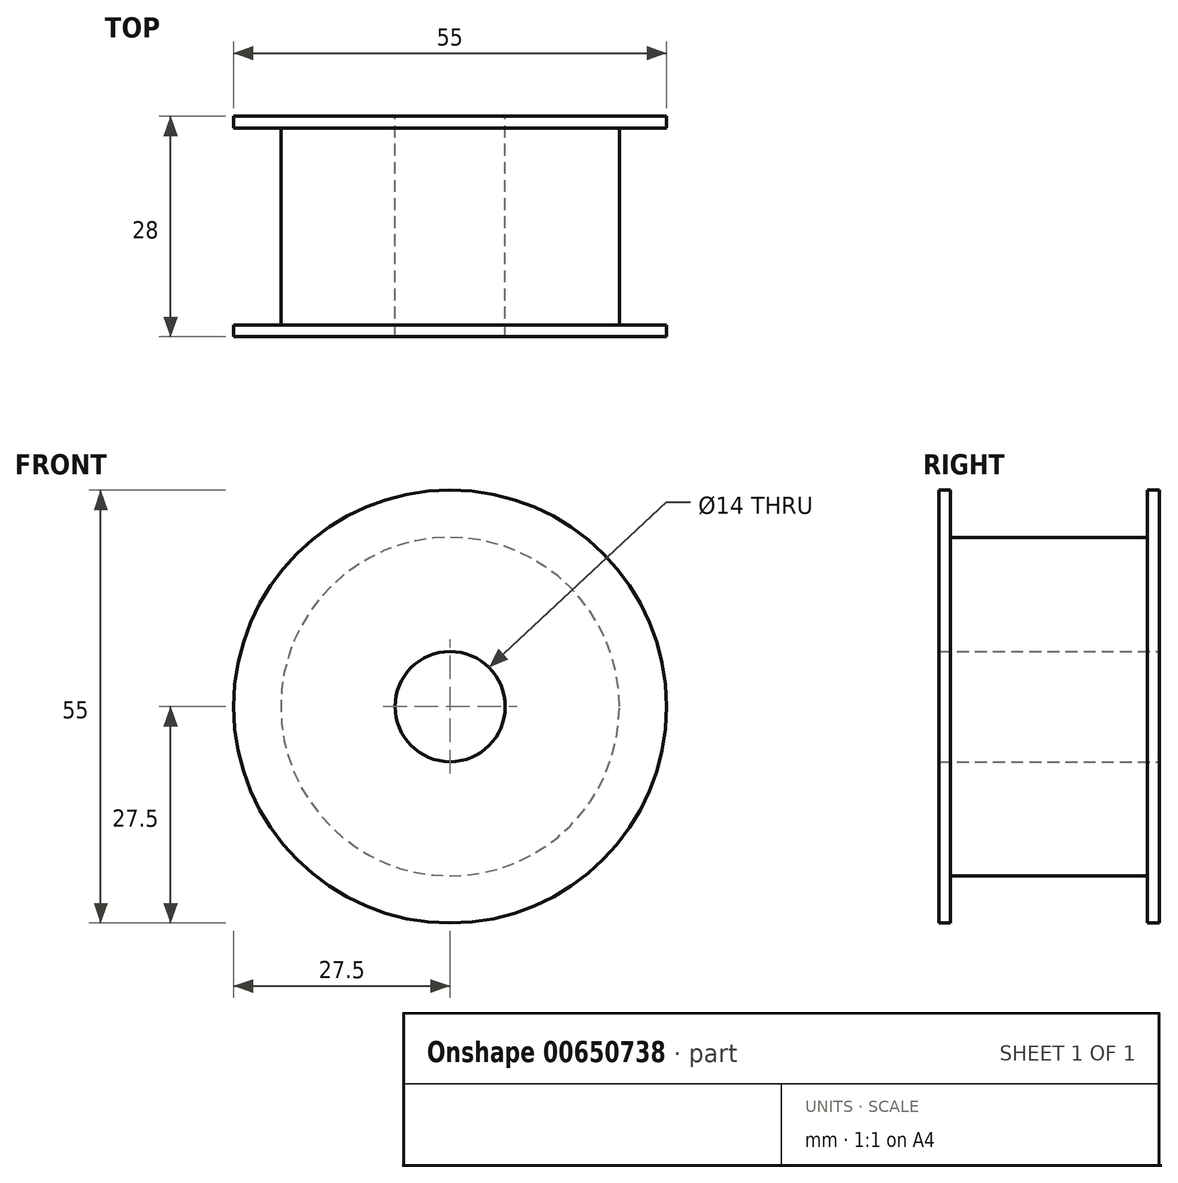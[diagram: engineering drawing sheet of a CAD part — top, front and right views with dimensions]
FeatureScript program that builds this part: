
annotation { "Feature Type Name" : "Feature", "Feature Type Description" : "" }
export const myFeature = defineFeature(function(context is Context, id is Id, definition is map)
    precondition{}
    {
        {
            var Q0;
            Q0=qCreatedBy(makeId("Front.planeOp"),FACE);
            var sketch = newSketch(context, id + "F0", { "sketchPlane" : qUnion([Q0])});
            skCircle(sketch, "E0", {"center": v(0, 0) * mm, "radius": 27.5 * mm});
            skSolve(sketch);
        }
        {
            var Q0;
            Q0 = qSketchRegion(id + "F0", true);
            extrude(context, id + "F1", {"entities" : qUnion([Q0]), "depth" : 28 * mm, "offsetDistance" : 25 * mm});
        }
        {
            var Q0;
            Q0=qCreatedBy(makeId("Right.planeOp"),FACE);
            var sketch = newSketch(context, id + "F2", { "sketchPlane" : qUnion([Q0])});
            skLineSegment(sketch, "E1.0", {"start": v(-28, -27.5) * mm, "end": v(-28, 27.5) * mm});
            skLineSegment(sketch, "E1.1", {"start": v(0, -27.5) * mm, "end": v(0, 27.5) * mm});
            skLineSegment(sketch, "E2", {"start": v(0, 0) * mm, "end": v(-28, 0) * mm, "construction": true});
            skLineSegment(sketch, "E3.bottom", {"start": v(-26.5, 27.5) * mm, "end": v(-1.5, 27.5) * mm});
            skLineSegment(sketch, "E3.top", {"start": v(-26.5, 21.5) * mm, "end": v(-1.5, 21.5) * mm});
            skLineSegment(sketch, "E3.left", {"start": v(-26.5, 27.5) * mm, "end": v(-26.5, 21.5) * mm});
            skLineSegment(sketch, "E3.right", {"start": v(-1.5, 27.5) * mm, "end": v(-1.5, 21.5) * mm});
            skPoint(sketch, "E4", {"position": v(-14, 21.5) * mm});
            skPoint(sketch, "E5", {"position": v(-14, 0) * mm});
            skSolve(sketch);
        }
        {
            var Q0;
            Q0 = qSketchRegion(id + "F2", true);
            var Q1;
            Q1=makeQuery(id+"F1.opExtrude","SWEPT_FACE",FACE,{"disambiguationData":[OSD([sQuery(id+"F0.wireOp",EDGE,"E0")])]});
            revolve(context, id + "F3", {"operationType" : NewBodyOperationType.REMOVE, "entities" : qUnion([Q0]), "axis" : qUnion([Q1]), "revolveType" : RevolveType.FULL, "oppositeDirection" : true});
        }
        {
            var Q0;
            Q0=qCreatedBy(makeId("Front.planeOp"),FACE);
            var sketch = newSketch(context, id + "F4", { "sketchPlane" : qUnion([Q0])});
            skCircle(sketch, "E6", {"center": v(0, 0) * mm, "radius": 7 * mm});
            skSolve(sketch);
        }
        {
            var Q0;
            Q0 = qSketchRegion(id + "F4", true);
            extrude(context, id + "F5", {"entities" : qUnion([Q0]), "operationType" : NewBodyOperationType.REMOVE, "endBound" : BoundingType.THROUGH_ALL, "depth" : 25 * mm, "offsetDistance" : 25 * mm});
        }
    });
